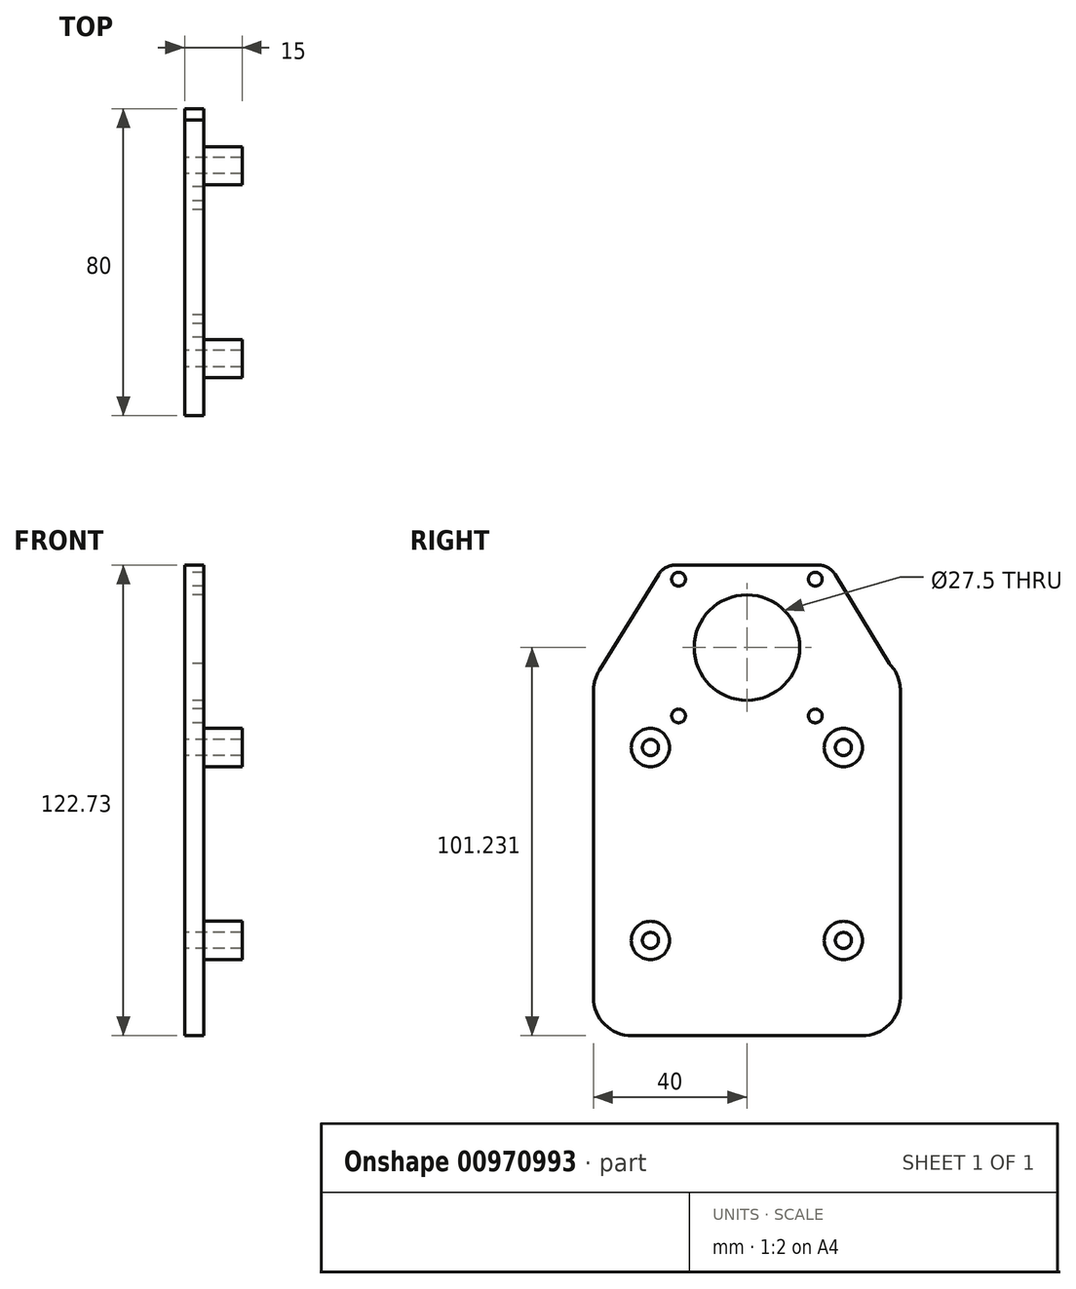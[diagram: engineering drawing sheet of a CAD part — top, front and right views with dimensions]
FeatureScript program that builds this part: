
annotation { "Feature Type Name" : "Feature", "Feature Type Description" : "" }
export const myFeature = defineFeature(function(context is Context, id is Id, definition is map)
    precondition{}
    {
        {
            var Q0;
            Q0=qCreatedBy(makeId("Right.planeOp"),FACE);
            var sketch = newSketch(context, id + "F0", { "sketchPlane" : qUnion([Q0])});
            skCircle(sketch, "E0", {"center": v(25.15, 0) * mm, "radius": 2.1 * mm});
            skCircle(sketch, "E1", {"center": v(-25.15, 0) * mm, "radius": 2.1 * mm});
            skCircle(sketch, "E2", {"center": v(25.15, -50.3) * mm, "radius": 2.1 * mm});
            skCircle(sketch, "E3", {"center": v(-25.15, -50.3) * mm, "radius": 2.1 * mm});
            skLineSegment(sketch, "E4", {"start": v(-25.15, 0) * mm, "end": v(25.15, -50.3) * mm, "construction": true});
            skLineSegment(sketch, "E5", {"start": v(25.15, 0) * mm, "end": v(-25.15, -50.3) * mm, "construction": true});
            skLineSegment(sketch, "E6.bottom", {"start": v(30, -75.15) * mm, "end": v(-30, -75.15) * mm});
            skLineSegment(sketch, "E6.top", {"start": v(30, 24.85) * mm, "end": v(-30, 24.85) * mm});
            skLineSegment(sketch, "E6.left", {"start": v(40, -65.15) * mm, "end": v(40, 14.85) * mm});
            skLineSegment(sketch, "E6.right", {"start": v(-40, -65.15) * mm, "end": v(-40, 14.85) * mm});
            skPoint(sketch, "E6.middle", {"position": v(0, -25.15) * mm});
            skPoint(sketch, "E7.visualSharp", {"position": v(-40, 24.85) * mm});
            skArc(sketch, "E7.filletArc", {"start": v(-30, 24.85) * mm, "mid": v(-37.07, 21.92) * mm, "end": v(-40, 14.85) * mm});
            skPoint(sketch, "E8.visualSharp", {"position": v(40, 24.85) * mm});
            skArc(sketch, "E8.filletArc", {"start": v(40, 14.85) * mm, "mid": v(37.07, 21.92) * mm, "end": v(30, 24.85) * mm});
            skPoint(sketch, "E9.visualSharp", {"position": v(40, -75.15) * mm});
            skArc(sketch, "E9.filletArc", {"start": v(30, -75.15) * mm, "mid": v(37.07, -72.22) * mm, "end": v(40, -65.15) * mm});
            skPoint(sketch, "E10.visualSharp", {"position": v(-40, -75.15) * mm});
            skArc(sketch, "E10.filletArc", {"start": v(-40, -65.15) * mm, "mid": v(-37.07, -72.22) * mm, "end": v(-30, -75.15) * mm});
            skLineSegment(sketch, "E11.bottom", {"start": v(21.5, 4.58) * mm, "end": v(-21.5, 4.58) * mm});
            skLineSegment(sketch, "E11.top", {"start": v(18.69, 47.58) * mm, "end": v(-18.71, 47.58) * mm});
            skLineSegment(sketch, "E11.left", {"start": v(21.5, 4.58) * mm, "end": v(21.5, 47.58) * mm});
            skLineSegment(sketch, "E11.right", {"start": v(-21.5, 4.58) * mm, "end": v(-21.5, 47.58) * mm});
            skPoint(sketch, "E11.middle", {"position": v(0, 26.08) * mm});
            skCircle(sketch, "E12", {"center": v(0, 26.08) * mm, "radius": 13.75 * mm});
            skCircle(sketch, "E13", {"center": v(25.15, 0) * mm, "radius": 12.5 * mm, "construction": true});
            skCircle(sketch, "E14", {"center": v(-25.15, 0) * mm, "radius": 12.5 * mm, "construction": true});
            skCircle(sketch, "E15", {"center": v(0, 26.08) * mm, "radius": 8.5 * mm, "construction": true});
            skPoint(sketch, "E16", {"position": v(0, 24.85) * mm});
            skLineSegment(sketch, "E17", {"start": v(-22.97, 45.21) * mm, "end": v(-38.5, 20.11) * mm});
            skLineSegment(sketch, "E18", {"start": v(22.96, 45.18) * mm, "end": v(37.07, 21.92) * mm});
            skLineSegment(sketch, "E19", {"start": v(-21.5, 47.58) * mm, "end": v(21.5, 4.58) * mm, "construction": true});
            skLineSegment(sketch, "E20", {"start": v(21.5, 47.58) * mm, "end": v(-21.5, 4.58) * mm, "construction": true});
            skCircle(sketch, "E21", {"center": v(17.83, 43.9) * mm, "radius": 1.8 * mm});
            skCircle(sketch, "E22", {"center": v(-17.83, 43.9) * mm, "radius": 1.8 * mm});
            skCircle(sketch, "E23", {"center": v(17.83, 8.26) * mm, "radius": 1.8 * mm});
            skCircle(sketch, "E24", {"center": v(-17.83, 8.26) * mm, "radius": 1.8 * mm});
            skCircle(sketch, "E25", {"center": v(25.15, 0) * mm, "radius": 5 * mm});
            skCircle(sketch, "E26", {"center": v(-25.15, 0) * mm, "radius": 5 * mm});
            skCircle(sketch, "E27", {"center": v(-25.15, -50.3) * mm, "radius": 5 * mm});
            skCircle(sketch, "E28", {"center": v(25.15, -50.3) * mm, "radius": 5 * mm});
            skPoint(sketch, "E29.visualSharp", {"position": v(-21.5, 47.58) * mm});
            skArc(sketch, "E29.filletArc", {"start": v(-18.71, 47.58) * mm, "mid": v(-21.15, 46.95) * mm, "end": v(-22.97, 45.21) * mm});
            skPoint(sketch, "E30.visualSharp", {"position": v(21.5, 47.58) * mm});
            skArc(sketch, "E30.filletArc", {"start": v(22.96, 45.18) * mm, "mid": v(21.14, 46.94) * mm, "end": v(18.69, 47.58) * mm});
            skSolve(sketch);
        }
        {
            var Q0;
            Q0 = qSketchRegion(id + "F0", true);
            var Q1;
            {var subQ1=sQuery(id+"F0.wireOp",EDGE,"E11.bottom");Q1=makeQuery(id+"F0.imprint","IMPRINT",FACE,{"disambiguationData":[TD([[makeQuery(id+"F0.imprint","IMPRINT",EDGE,{"derivedFrom":subQ1}),-1.0]])]});}
            extrude(context, id + "F1", {"entities" : qUnion([Q0, Q1]), "depth" : 5 * mm, "offsetDistance" : 25 * mm});
        }
        {
            var Q0;
            Q0=makeQuery(id+"F0.imprint","IMPRINT",FACE,{"disambiguationData":[TD([[makeQuery(id+"F0.imprint","IMPRINT",EDGE,{"derivedFrom":sQuery(id+"F0.wireOp",EDGE,"E1")}),-1.0]])]});
            var Q1;
            Q1=makeQuery(id+"F0.imprint","IMPRINT",FACE,{"disambiguationData":[TD([[makeQuery(id+"F0.imprint","IMPRINT",EDGE,{"derivedFrom":sQuery(id+"F0.wireOp",EDGE,"E0")}),-1.0]])]});
            var Q2;
            Q2=makeQuery(id+"F0.imprint","IMPRINT",FACE,{"disambiguationData":[TD([[makeQuery(id+"F0.imprint","IMPRINT",EDGE,{"derivedFrom":sQuery(id+"F0.wireOp",EDGE,"E2")}),-1.0]])]});
            var Q3;
            Q3=makeQuery(id+"F0.imprint","IMPRINT",FACE,{"disambiguationData":[TD([[makeQuery(id+"F0.imprint","IMPRINT",EDGE,{"derivedFrom":sQuery(id+"F0.wireOp",EDGE,"E3")}),-1.0]])]});
            extrude(context, id + "F2", {"entities" : qUnion([Q0, Q1, Q2, Q3]), "operationType" : NewBodyOperationType.ADD, "depth" : 15 * mm, "offsetDistance" : 25 * mm});
        }
    });
